# Revit family: Sink-Bathroom_Vessel-KOHLER-Reve-K-4819
name_source: partatom
category: Plumbing Fixtures
revit_build: Autodesk Revit 2015 (Build: 20140606_1530(x64)
units: mm (PartAtom-declared; Revit-internal decimal feet)

## types (3) — shared parameters
ADA = No
Assembly Code = D2010400
Cold Water Inlet = Cold Water Inlet
Date Modified = 12/26/2017
Default Elevation = 36"
Description = Above-counter Bathroom Sink
Height = 4 7/16"
Hot Water Inlet = Hot Water Inlet
Length = 21 7/16"
Manufacturer = KOHLER Co.
MasterFormat 1995 = 15410
MasterFormat 2004 = 22.41.16
Material = Fireclay
Product Documentation Link = http://www.us.kohler.com
Product Name = Rêve
Product Page URL = http://www.us.kohler.com
URL = https://www.us.kohler.com
Waste Connection = Yes
Waste Water Outlet = Waste Water Outlet
Width = 14 27/32"

## per-type parameters (varying)
| type | Finish | Model | Type |
| 0-White | Kohler-Fireclay-0-White | K-4819-0 | 1 |
| 96-Biscuit | Kohler-Fireclay-96-Biscuit | K-4819-96 | 2 |
| 47-Almond | Kohler-Fireclay-47-Almond | K-4819-47 | 3 |

## geometry (parser evidence)
native form markers: Sweep x6
no freeform markers — native parametric forms only
